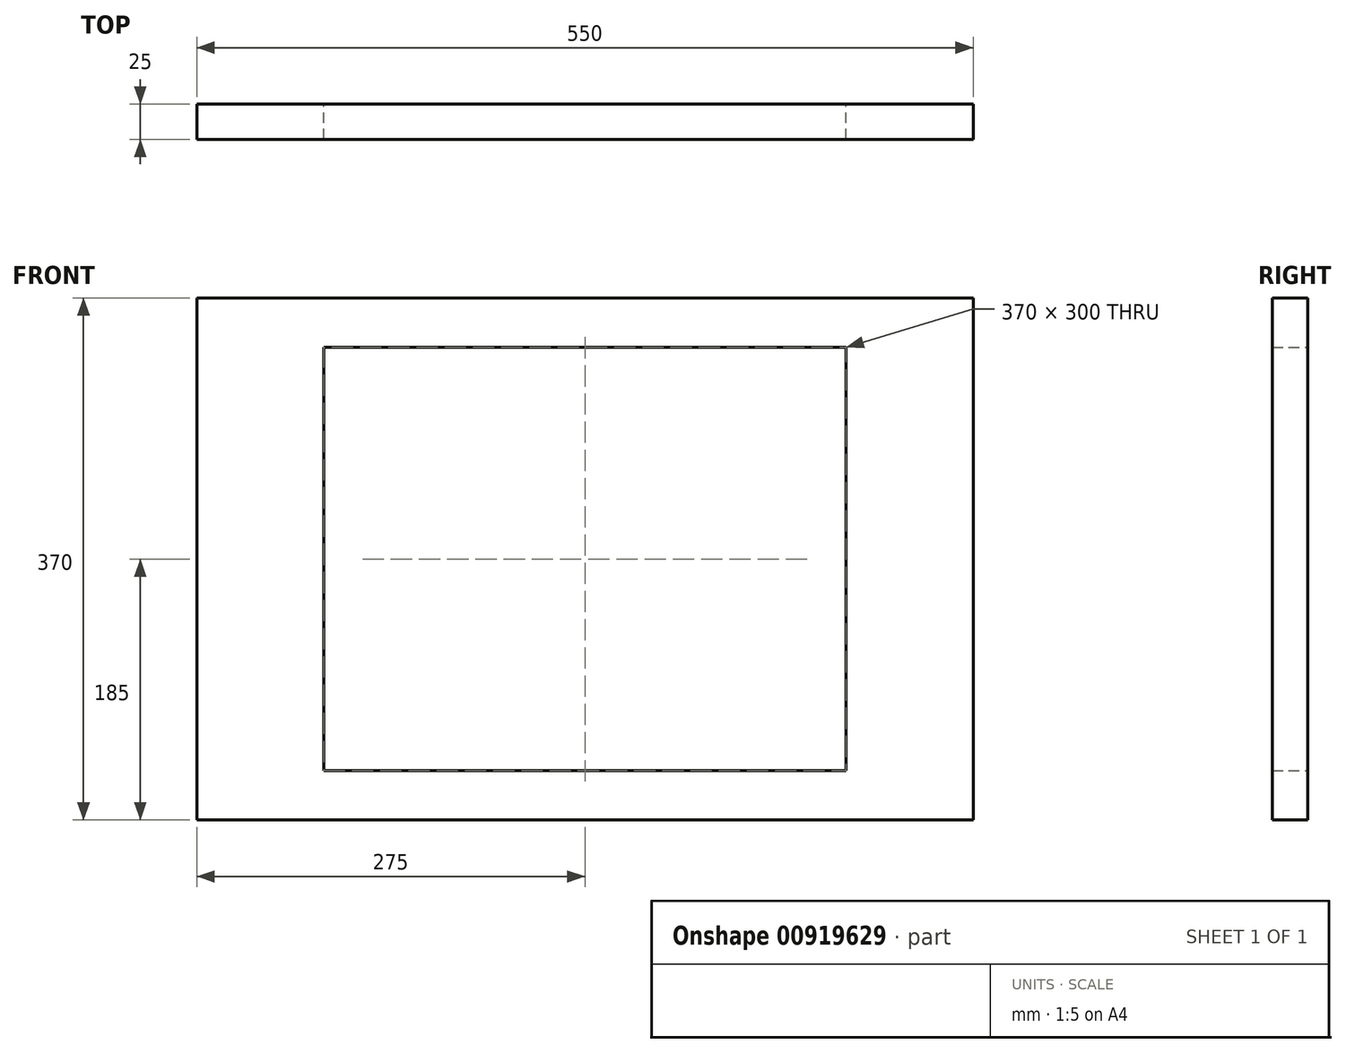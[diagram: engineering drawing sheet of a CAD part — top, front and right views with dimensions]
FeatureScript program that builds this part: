
annotation { "Feature Type Name" : "Feature", "Feature Type Description" : "" }
export const myFeature = defineFeature(function(context is Context, id is Id, definition is map)
    precondition{}
    {
        {
            var Q0;
            Q0=qCreatedBy(makeId("Front.planeOp"),FACE);
            var sketch = newSketch(context, id + "F0", { "sketchPlane" : qUnion([Q0])});
            skLineSegment(sketch, "E0.rect.bottom", {"start": v(275, -185) * mm, "end": v(-275, -185) * mm});
            skLineSegment(sketch, "E0.rect.top", {"start": v(275, 185) * mm, "end": v(-275, 185) * mm});
            skLineSegment(sketch, "E0.rect.left", {"start": v(275, -185) * mm, "end": v(275, 185) * mm});
            skLineSegment(sketch, "E0.rect.right", {"start": v(-275, -185) * mm, "end": v(-275, 185) * mm});
            skPoint(sketch, "E0.rect.middle", {"position": v(0, 0) * mm});
            skLineSegment(sketch, "E1.rect.bottom", {"start": v(185, -150) * mm, "end": v(-185, -150) * mm});
            skLineSegment(sketch, "E1.rect.top", {"start": v(185, 150) * mm, "end": v(-185, 150) * mm});
            skLineSegment(sketch, "E1.rect.left", {"start": v(185, -150) * mm, "end": v(185, 150) * mm});
            skLineSegment(sketch, "E1.rect.right", {"start": v(-185, -150) * mm, "end": v(-185, 150) * mm});
            skSolve(sketch);
        }
        {
            var Q0;
            Q0=qSketchRegion(id+"F0",true);
            extrude(context, id + "F1", {"entities" : qUnion([Q0]), "depth" : 25 * mm});
        }
    });
